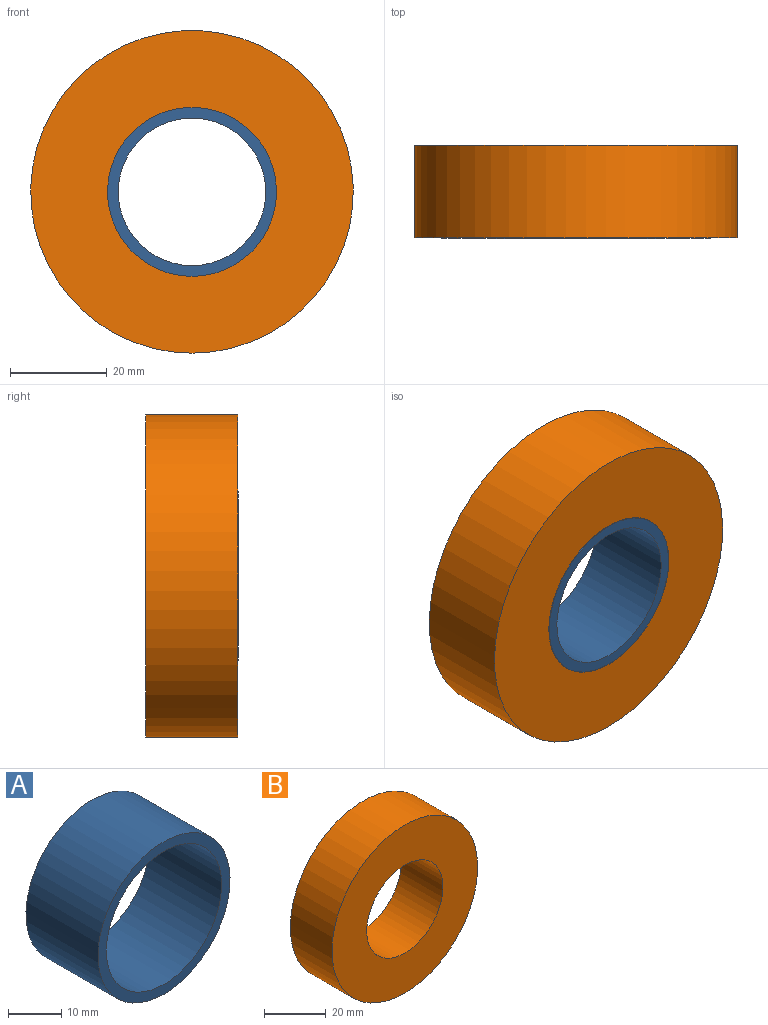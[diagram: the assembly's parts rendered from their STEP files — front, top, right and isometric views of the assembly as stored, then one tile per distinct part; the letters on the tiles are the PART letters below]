
ASSEMBLY  parts=2 mates=1
PART A: 4 faces, bbox 34.9x19.1x34.9 mm
  f0: cylinder r=15.24mm len=30.48mm, axis (0,1,0), area 1824.1mm2, adj f2,f3
  f1: cylinder r=17.46mm len=34.93mm, axis (0,1,0), area 2090.2mm2, adj f2,f3
  f2: plane 34.93x34.93mm, normal (0,-1,0), area 228.3mm2, adj f0,f1
  f3: plane 34.93x34.93mm, normal (0,1,0), area 228.3mm2, adj f0,f1
PART B: 4 faces, bbox 66.7x19.1x66.7 mm
  f0: cylinder r=17.46mm len=34.93mm, axis (0,1,0), area 2090.2mm2, adj f2,f3
  f1: cylinder r=33.34mm len=66.68mm, axis (0,1,0), area 3990.3mm2, adj f2,f3
  f2: plane 66.68x66.68mm, normal (0,-1,0), area 2533.5mm2, adj f0,f1
  f3: plane 66.68x66.68mm, normal (0,1,0), area 2533.5mm2, adj f0,f1
PLACE A t=(-10.81,8.73,-2.77)mm
PLACE B t=(-10.81,8.86,-2.77)mm
MATE fastened A.f1 <-> B.f1  axis (0,1,0) through (-10.81,-0.79,-2.77)mm
